# Revit family: Faucet-Lavatory-KOHLER-PARALLEL-K-23484T
name_source: partatom
category: Plumbing Fixtures
revit_build: Autodesk Revit 2017 (Build: 20160225_1515(x64)
units: mm (PartAtom-declared; Revit-internal decimal feet)

## family parameters
Cut with Voids When Loaded = No
Host = Face
OmniClass Number = 23.31.11.00
OmniClass Title = Faucets
Part Type = Normal
Room Calculation Point = No
Round Connector Dimension = Use Diameter
Shared = No

## types (5) — shared parameters
ADA Compliant = No
Assembly Code = D2010
CW Connection = Yes
Cold Water Inlet = Cold Water Inlet
Date Modified = 05/18/2020
Default Elevation = 36"
Description = 8 inch Washbasin Faucet
Flow Rate = 0 GPM
HW Connection = Yes
Handle Clearance = 2 7/16"
Height = 6"
Hot Water Inlet = Hot Water Inlet
Length = 5 1/16"
Manufacturer = KOHLER Co.
MasterFormat 1995 = 15410
MasterFormat 2004 = 22.41.39
Material = Premium Metal Construction
Pressure = 0.00 psi
Product Name = PARALLEL
Spout Reach = 5 1/16"
URL = http://www.kohler.com.cn
Vent Connection = No
Waste Connection = No
Waste Water Outlet = Waste Water Outlet
WaterSense Certified = No

## per-type parameters (varying)
| type | Drain Included | Finish | Model | Product Documentation Link | Product Page URL | Type |
| BN-Roman Silver | Yes | Kohler-Metal-BN-Roman_Silver | K-23484T-4-BN | http://files.kohler.com.cn | http://www.kohler.com.cn | 2 |
| RGD-Rose Gold | Yes | Kohler-Metal-RGD-Polished_Rose_Gold | K-23484T-4-RGD | http://files.kohler.com.cn | http://www.kohler.com.cn | 3 |
| AF-Flange Gold | Yes | Kohler-Metal-AF-Flange_Gold | K-23484T-4-AF | http://files.kohler.com.cn | http://www.kohler.com.cn | 4 |
| CP-Polished Chrome | Yes | Kohler-Metal-CP-Polished_Chrome | K-23484T-4-CP | http://files.kohler.com.cn | http://www.kohler.com.cn | 1 |
| Without Drain,CP-Polished Chrome | No | Kohler-Metal-CP-Polished_Chrome | K-23484T-4ND-CP |  |  | 5 |

## geometry (parser evidence)
native form markers: Sweep x9
no freeform markers — native parametric forms only
